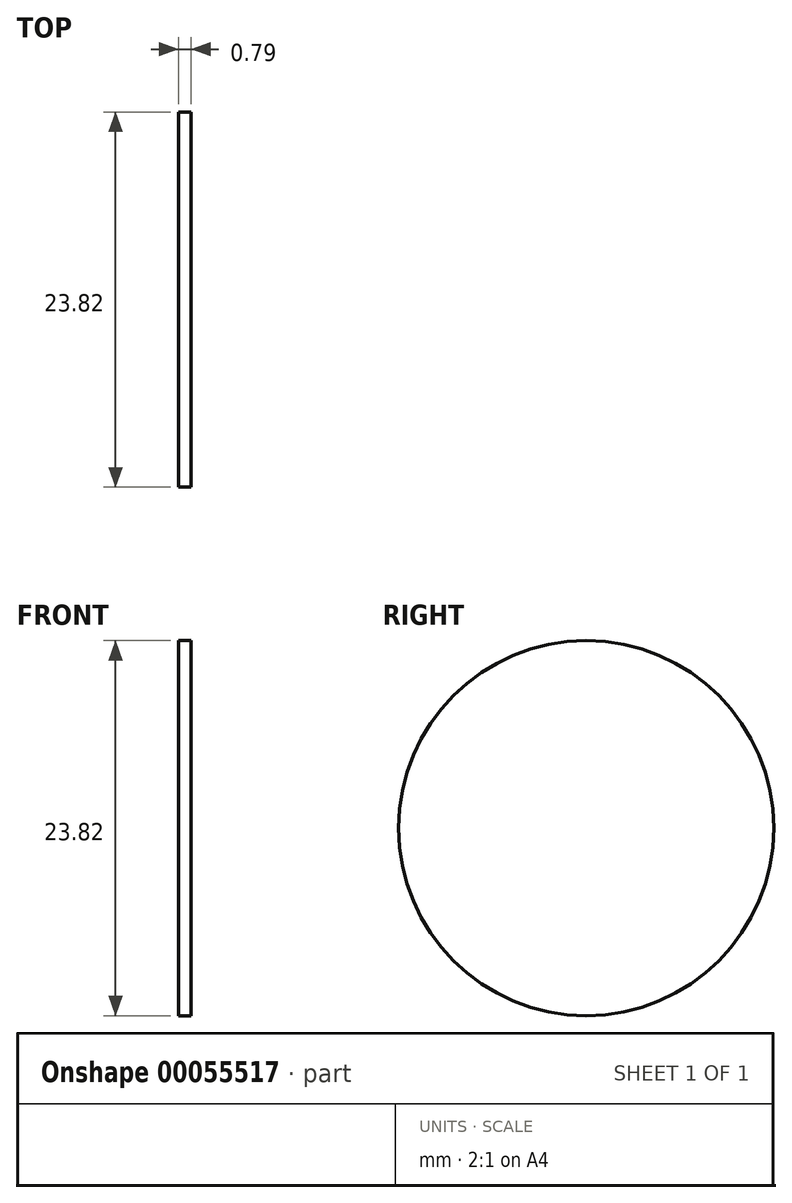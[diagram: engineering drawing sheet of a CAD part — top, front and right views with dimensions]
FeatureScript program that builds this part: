
annotation { "Feature Type Name" : "Feature", "Feature Type Description" : "" }
export const myFeature = defineFeature(function(context is Context, id is Id, definition is map)
    precondition{}
    {
        {
            var Q0;
            Q0=qCreatedBy(makeId("Right.planeOp"),FACE);
            var sketch = newSketch(context, id + "F0", { "sketchPlane" : qUnion([Q0])});
            skCircle(sketch, "E0", {"center": v(0, 0) * mm, "radius": 11.91 * mm});
            skSolve(sketch);
        }
        {
            var Q0;
            Q0 = qSketchRegion(id + "F0", true);
            extrude(context, id + "F1", {"entities" : qUnion([Q0]), "depth" : 0.8 * mm});
        }
    });
